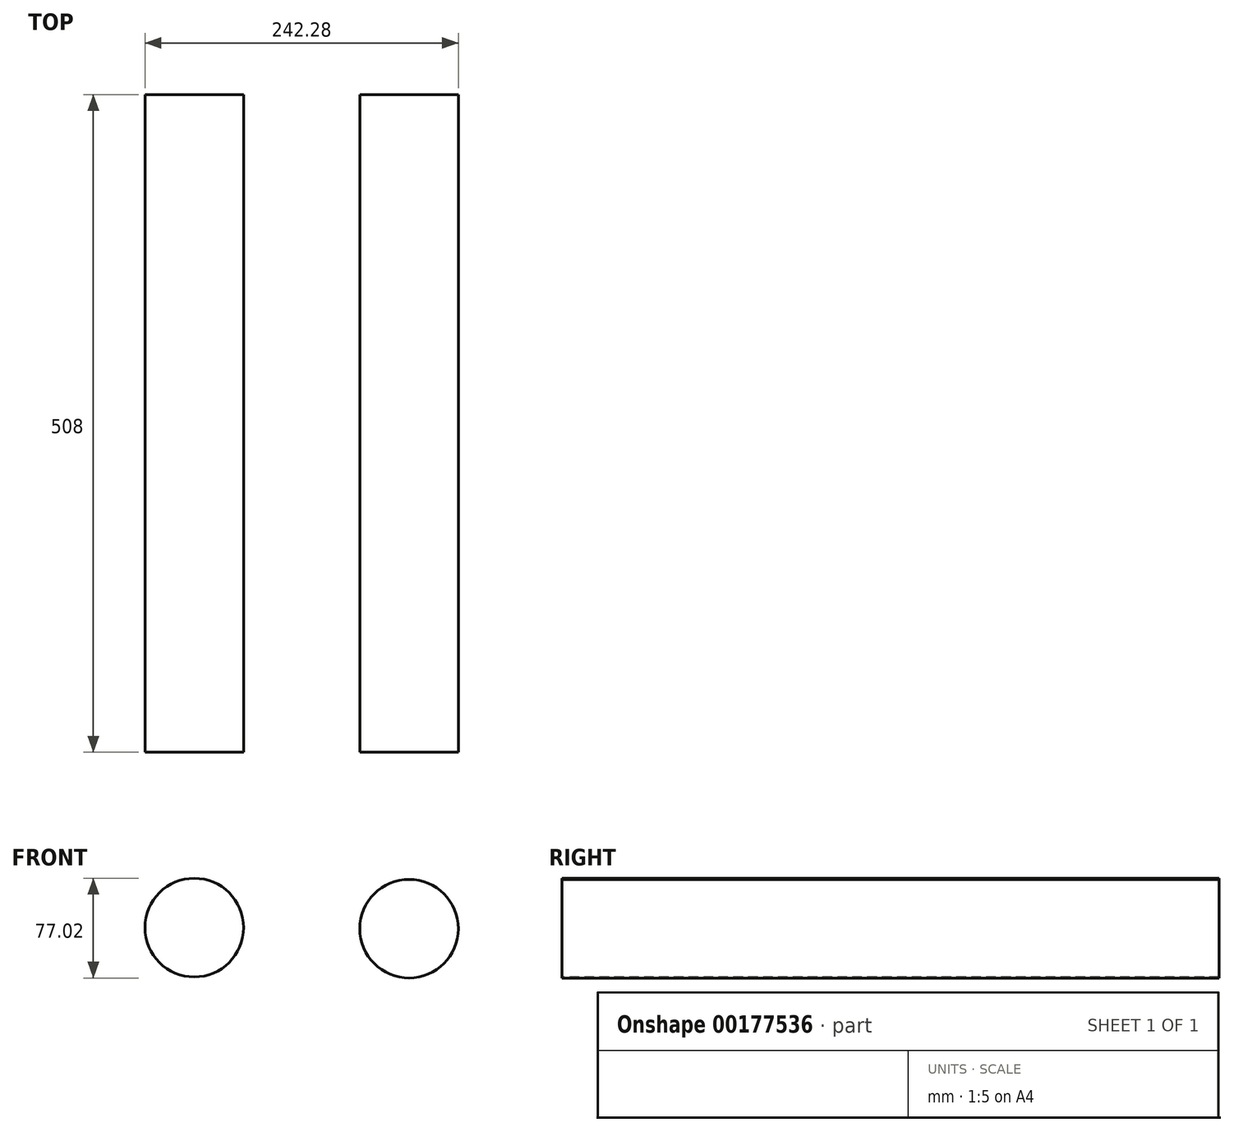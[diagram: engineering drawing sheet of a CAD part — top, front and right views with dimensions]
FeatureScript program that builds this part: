
annotation { "Feature Type Name" : "Feature", "Feature Type Description" : "" }
export const myFeature = defineFeature(function(context is Context, id is Id, definition is map)
    precondition{}
    {
        {
            var Q0;
            Q0=qCreatedBy(makeId("Front.planeOp"),FACE);
            var sketch = newSketch(context, id + "F0", { "sketchPlane" : qUnion([Q0])});
            skCircle(sketch, "E0", {"center": v(-90.18, 0.82) * mm, "radius": 38.1 * mm});
            skCircle(sketch, "E1", {"center": v(75.9, 0) * mm, "radius": 38.1 * mm});
            skSolve(sketch);
        }
        {
            var Q0;
            Q0=qSketchRegion(id+"F0",true);
            extrude(context, id + "F1", {"entities" : qUnion([Q0]), "oppositeDirection" : true, "depth" : 508 * mm});
        }
    });
